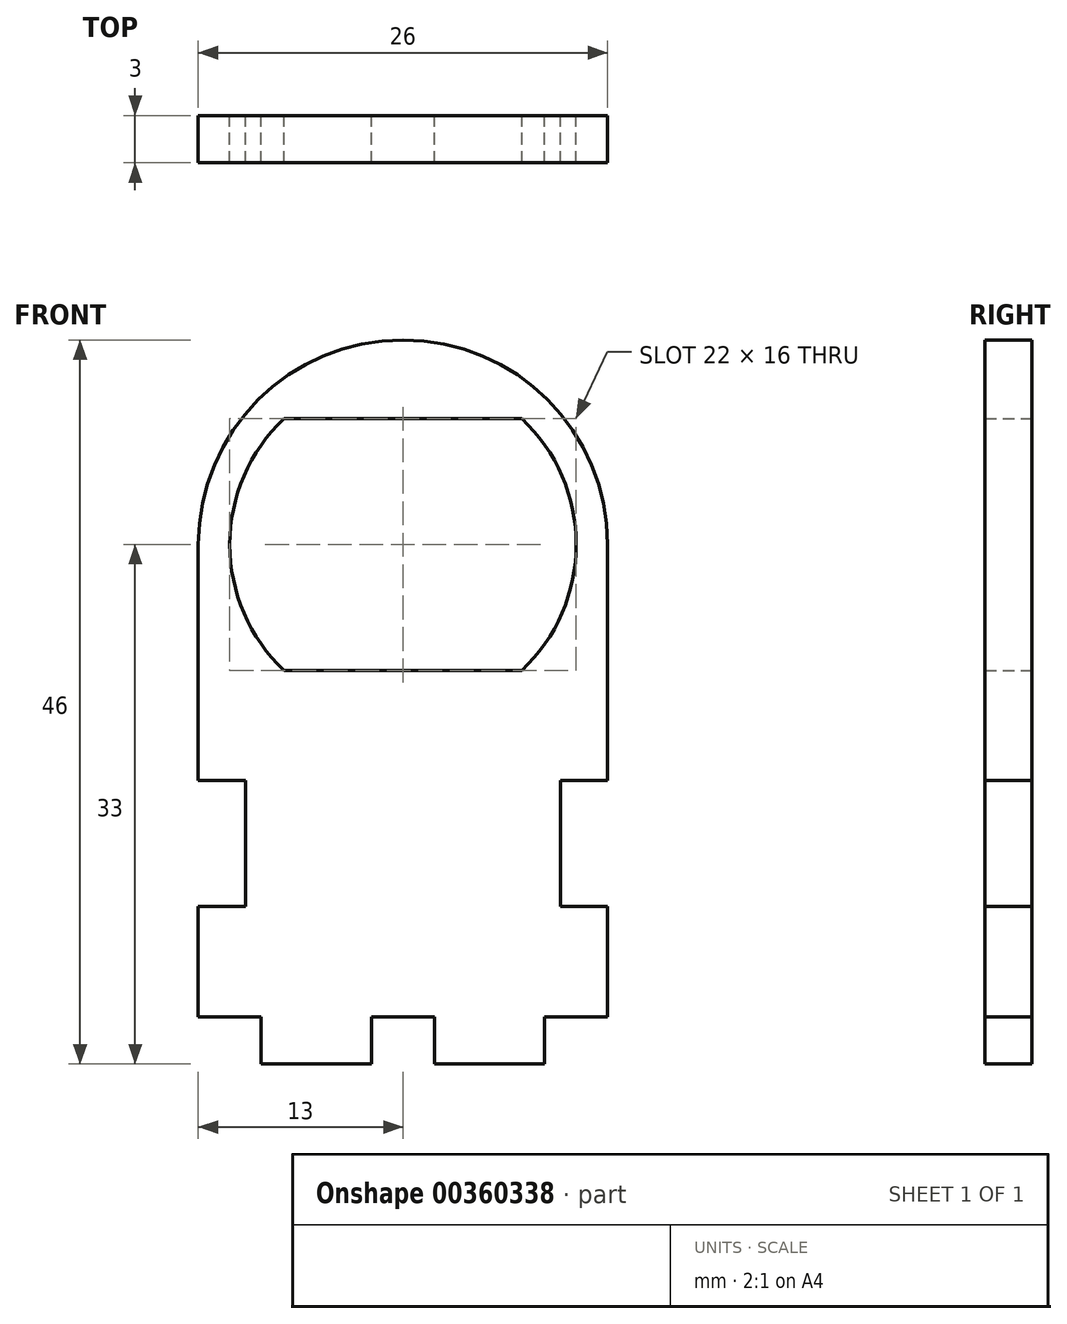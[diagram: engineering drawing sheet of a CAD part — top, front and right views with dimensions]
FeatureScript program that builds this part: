
annotation { "Feature Type Name" : "Feature", "Feature Type Description" : "" }
export const myFeature = defineFeature(function(context is Context, id is Id, definition is map)
    precondition{}
    {
        {
            var Q0;
            Q0=qCreatedBy(makeId("Front.planeOp"),FACE);
            var sketch = newSketch(context, id + "F0", { "sketchPlane" : qUnion([Q0])});
            skArc(sketch, "E0", {"start": v(13, 30) * mm, "mid": v(0, 43) * mm, "end": v(-13, 30) * mm});
            skLineSegment(sketch, "E1.bottom", {"start": v(-13, 30) * mm, "end": v(13, 30) * mm, "construction": true});
            skLineSegment(sketch, "E2", {"start": v(-13, 0) * mm, "end": v(-9, 0) * mm});
            skLineSegment(sketch, "E3", {"start": v(-9, 0) * mm, "end": v(-9, -3) * mm});
            skLineSegment(sketch, "E4", {"start": v(-9, -3) * mm, "end": v(-2, -3) * mm});
            skLineSegment(sketch, "E5", {"start": v(-2, -3) * mm, "end": v(-2, 0) * mm});
            skLineSegment(sketch, "E6", {"start": v(-2, 0) * mm, "end": v(0, 0) * mm});
            skLineSegment(sketch, "E7.MirrorCS", {"start": v(2, 0) * mm, "end": v(0, 0) * mm});
            skLineSegment(sketch, "E8.MirrorCS", {"start": v(2, -3) * mm, "end": v(2, 0) * mm});
            skLineSegment(sketch, "E9.MirrorCS", {"start": v(13, 0) * mm, "end": v(9, 0) * mm});
            skLineSegment(sketch, "E10.MirrorCS", {"start": v(9, -3) * mm, "end": v(2, -3) * mm});
            skLineSegment(sketch, "E11.MirrorCS", {"start": v(9, 0) * mm, "end": v(9, -3) * mm});
            skArc(sketch, "E12", {"start": v(-7.55, 38) * mm, "mid": v(-11, 30) * mm, "end": v(-7.55, 22) * mm});
            skArc(sketch, "E13", {"start": v(7.55, 38) * mm, "mid": v(11, 30) * mm, "end": v(7.55, 22) * mm});
            skLineSegment(sketch, "E14", {"start": v(-7.55, 38) * mm, "end": v(7.55, 38) * mm});
            skLineSegment(sketch, "E15", {"start": v(-7.55, 22) * mm, "end": v(7.55, 22) * mm});
            skLineSegment(sketch, "E16", {"start": v(-13, 30) * mm, "end": v(-13, 15) * mm});
            skLineSegment(sketch, "E17", {"start": v(-13, 15) * mm, "end": v(-10, 15) * mm});
            skLineSegment(sketch, "E18", {"start": v(-10, 15) * mm, "end": v(-10, 7) * mm});
            skLineSegment(sketch, "E19", {"start": v(-10, 7) * mm, "end": v(-13, 7) * mm});
            skLineSegment(sketch, "E20", {"start": v(-13, 7) * mm, "end": v(-13, 0) * mm});
            skLineSegment(sketch, "E21", {"start": v(13, 30) * mm, "end": v(13, 15) * mm});
            skLineSegment(sketch, "E22", {"start": v(13, 15) * mm, "end": v(10, 15) * mm});
            skLineSegment(sketch, "E23", {"start": v(10, 15) * mm, "end": v(10, 7) * mm});
            skLineSegment(sketch, "E24", {"start": v(10, 7) * mm, "end": v(13, 7) * mm});
            skLineSegment(sketch, "E25", {"start": v(13, 7) * mm, "end": v(13, 0) * mm});
            skSolve(sketch);
        }
        {
            var Q0;
            Q0=makeQuery(id+"F0.imprint","IMPRINT",FACE,{"disambiguationData":[TD([[makeQuery(id+"F0.imprint","IMPRINT",EDGE,{"derivedFrom":sQuery(id+"F0.wireOp",EDGE,"E0")}),1.0]])]});
            extrude(context, id + "F1", {"entities" : qUnion([Q0]), "depth" : 3 * mm});
        }
    });
